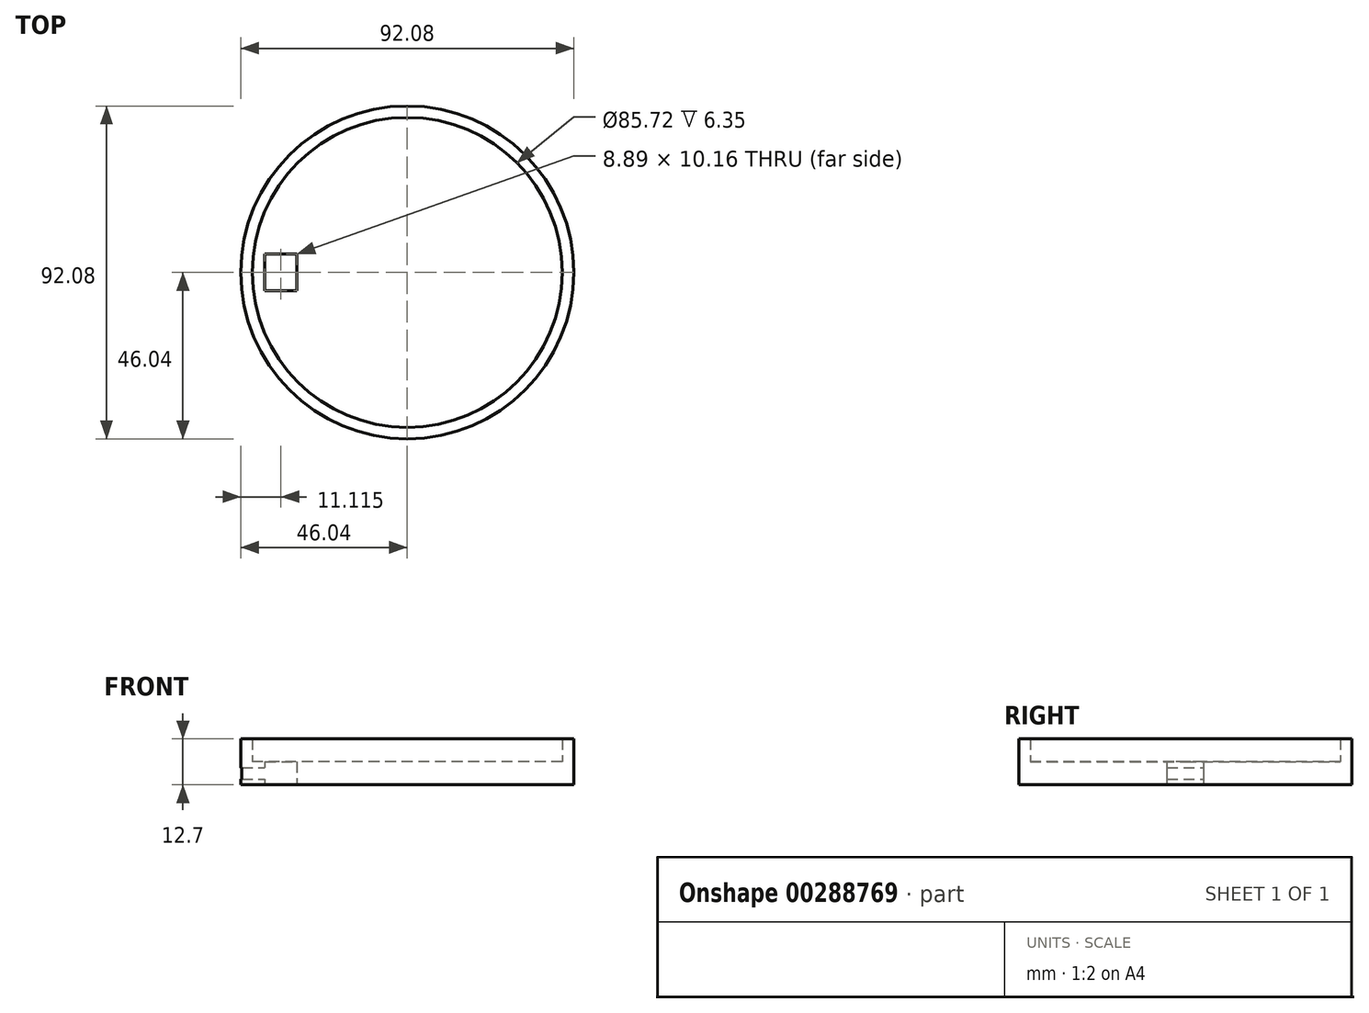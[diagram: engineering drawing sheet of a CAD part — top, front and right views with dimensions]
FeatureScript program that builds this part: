
annotation { "Feature Type Name" : "Feature", "Feature Type Description" : "" }
export const myFeature = defineFeature(function(context is Context, id is Id, definition is map)
    precondition{}
    {
        {
            var Q0;
            Q0=qCreatedBy(makeId("Top.planeOp"),FACE);
            var sketch = newSketch(context, id + "F0", { "sketchPlane" : qUnion([Q0])});
            skCircle(sketch, "E0", {"center": v(0, 0) * mm, "radius": 46.04 * mm});
            skCircle(sketch, "E1", {"center": v(0, 0) * mm, "radius": 42.86 * mm});
            skLineSegment(sketch, "E2.bottom", {"start": v(-39.37, 5.08) * mm, "end": v(-30.48, 5.08) * mm});
            skLineSegment(sketch, "E2.top", {"start": v(-39.37, -5.08) * mm, "end": v(-30.48, -5.08) * mm});
            skLineSegment(sketch, "E2.left", {"start": v(-39.37, 5.08) * mm, "end": v(-39.37, -5.08) * mm});
            skLineSegment(sketch, "E2.right", {"start": v(-30.48, 5.08) * mm, "end": v(-30.48, -5.08) * mm});
            skPoint(sketch, "E2.middle", {"position": v(-34.93, 0) * mm});
            skSolve(sketch);
        }
        {
            var Q0;
            Q0=makeQuery(id+"F0.imprint","IMPRINT",FACE,{"disambiguationData":[TD([[makeQuery(id+"F0.imprint","IMPRINT",EDGE,{"derivedFrom":sQuery(id+"F0.wireOp",EDGE,"E0")}),1.0]])]});
            extrude(context, id + "F1", {"entities" : qUnion([Q0]), "depth" : 12.7 * mm});
        }
        {
            var Q0;
            Q0=makeQuery(id+"F0.imprint","IMPRINT",FACE,{"disambiguationData":[TD([[makeQuery(id+"F0.imprint","IMPRINT",EDGE,{"derivedFrom":sQuery(id+"F0.wireOp",EDGE,"E1")}),1.0]])]});
            extrude(context, id + "F2", {"entities" : qUnion([Q0]), "operationType" : NewBodyOperationType.ADD, "depth" : 6.35 * mm});
        }
        {
            var Q0;
            Q0=makeQuery(id+"F2.opExtrude","SWEPT_FACE",FACE,{"disambiguationData":[OSD([sQuery(id+"F0.wireOp",EDGE,"E2.left")])]});
            var sketch = newSketch(context, id + "F3", { "sketchPlane" : qUnion([Q0])});
            skLineSegment(sketch, "E3", {"start": v(-5.08, 1.59) * mm, "end": v(5.08, 1.59) * mm});
            skLineSegment(sketch, "E4", {"start": v(-5.08, 4.76) * mm, "end": v(5.08, 4.76) * mm});
            skSolve(sketch);
        }
        {
            var Q0;
            {var subQ0=sQuery(id+"F3.wireOp",EDGE,"E3");Q0=makeQuery(id+"F3.imprint","IMPRINT",FACE,{"disambiguationData":[TD([[makeQuery(id+"F3.imprint","IMPRINT",EDGE,{"derivedFrom":subQ0}),1.0]])]});}
            extrude(context, id + "F4", {"entities" : qUnion([Q0]), "operationType" : NewBodyOperationType.REMOVE, "endBound" : BoundingType.THROUGH_ALL, "oppositeDirection" : true, "depth" : 25.4 * mm});
        }
    });
